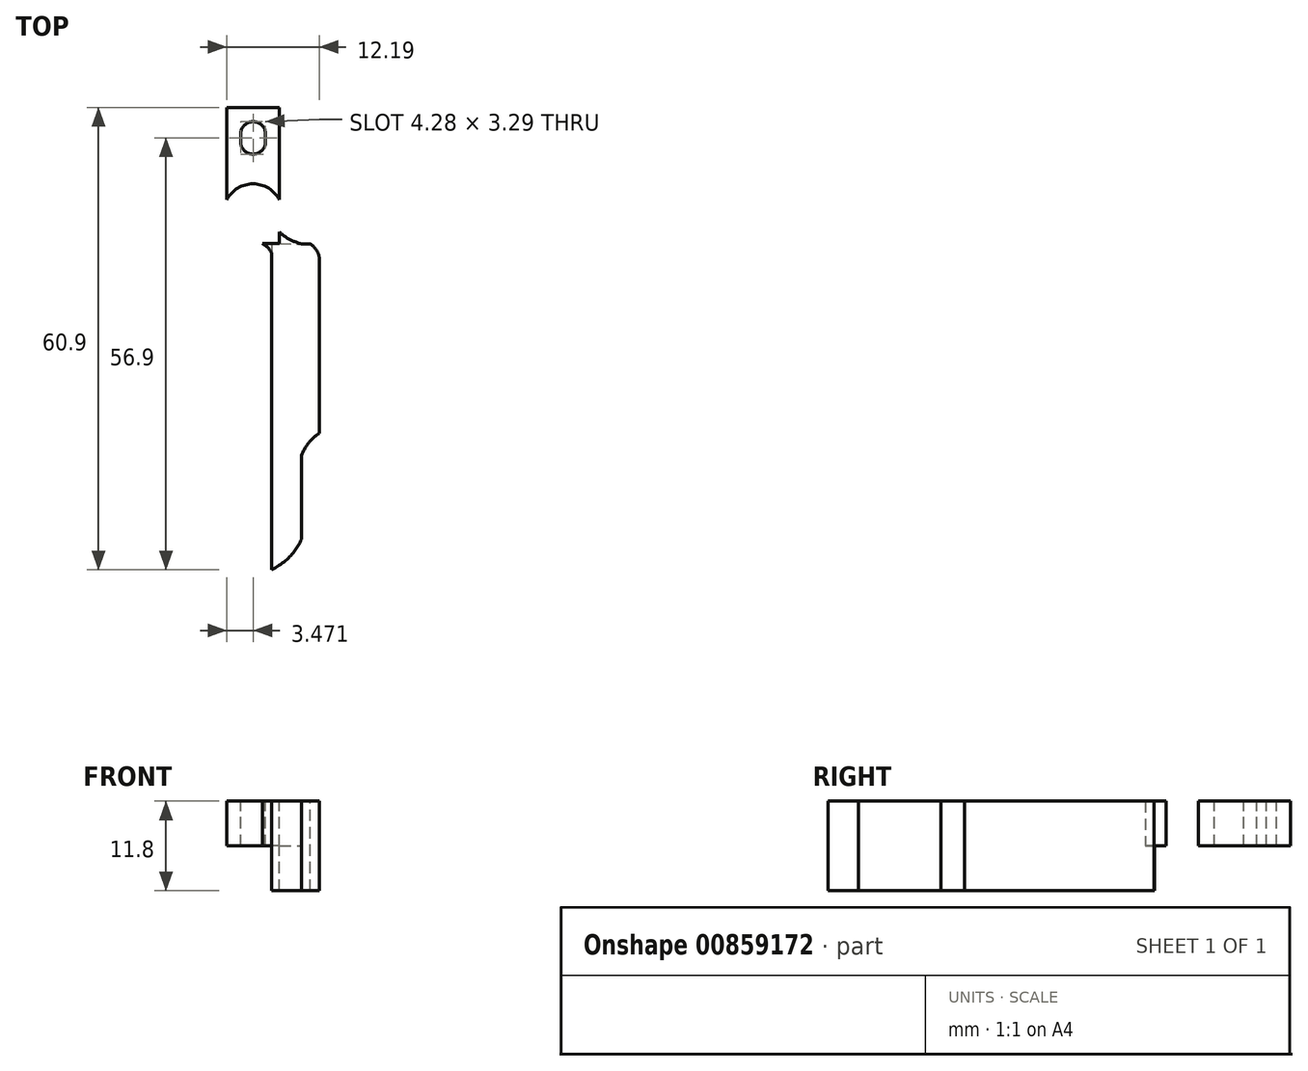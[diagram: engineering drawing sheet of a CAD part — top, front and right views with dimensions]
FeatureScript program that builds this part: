
annotation { "Feature Type Name" : "Feature", "Feature Type Description" : "" }
export const myFeature = defineFeature(function(context is Context, id is Id, definition is map)
    precondition{}
    {
        {
            var Q0;
            Q0=qCreatedBy(makeId("Top.planeOp"),FACE);
            var sketch = newSketch(context, id + "F0", { "sketchPlane" : qUnion([Q0])});
            skLineSegment(sketch, "E0.bottom", {"start": v(0, 0) * mm, "end": v(6.95, 0) * mm});
            skLineSegment(sketch, "E0.top", {"start": v(0, 17.9) * mm, "end": v(6.95, 17.9) * mm});
            skLineSegment(sketch, "E0.left", {"start": v(0, 0) * mm, "end": v(0, 17.9) * mm});
            skLineSegment(sketch, "E0.right", {"start": v(6.95, 0) * mm, "end": v(6.95, 17.9) * mm});
            skLineSegment(sketch, "E1", {"start": v(0, 0) * mm, "end": v(0, 7.85) * mm});
            skLineSegment(sketch, "E2", {"start": v(3.48, 0) * mm, "end": v(3.48, 7.85) * mm});
            skLineSegment(sketch, "E3", {"start": v(3.48, 7.85) * mm, "end": v(3.48, 6.9) * mm});
            skCircle(sketch, "E4", {"center": v(3.48, 3.92) * mm, "radius": 3.92 * mm});
            skLineSegment(sketch, "E5", {"start": v(3.47, 17.9) * mm, "end": v(3.47, 16.05) * mm});
            skLineSegment(sketch, "E6", {"start": v(3.47, 16.05) * mm, "end": v(3.48, 11.75) * mm});
            skLineSegment(sketch, "E7", {"start": v(3.47, 13.9) * mm, "end": v(3.47, 16.05) * mm});
            skLineSegment(sketch, "E8", {"start": v(3.48, 11.75) * mm, "end": v(3.47, 13.9) * mm});
            skLineSegment(sketch, "E9", {"start": v(4.55, 12.83) * mm, "end": v(4.55, 14.98) * mm});
            skLineSegment(sketch, "E10.bottom", {"start": v(3.48, 0) * mm, "end": v(1.03, 0) * mm});
            skLineSegment(sketch, "E10.top", {"start": v(3.48, -100) * mm, "end": v(1.03, -100) * mm});
            skLineSegment(sketch, "E10.left", {"start": v(3.48, 0) * mm, "end": v(3.48, -100) * mm});
            skLineSegment(sketch, "E10.right", {"start": v(1.03, 0) * mm, "end": v(1.03, -100) * mm});
            skLineSegment(sketch, "E11.bottom", {"start": v(3.48, 0) * mm, "end": v(5.93, 0) * mm});
            skLineSegment(sketch, "E11.top", {"start": v(3.48, -100) * mm, "end": v(5.93, -100) * mm});
            skLineSegment(sketch, "E11.right", {"start": v(5.93, 0) * mm, "end": v(5.93, -100) * mm});
            skLineSegment(sketch, "E12", {"start": v(5.93, 0) * mm, "end": v(5.93, 1.16) * mm});
            skLineSegment(sketch, "E13", {"start": v(1.03, 0) * mm, "end": v(1.02, 1.22) * mm});
            skLineSegment(sketch, "E14.bottom", {"start": v(6.95, 0) * mm, "end": v(9.83, -0.08) * mm});
            skLineSegment(sketch, "E14.left", {"start": v(6.95, 0) * mm, "end": v(6.95, 1.5) * mm});
            skLineSegment(sketch, "E15.right", {"start": v(5.93, -0.08) * mm, "end": v(5.93, -100) * mm});
            skLineSegment(sketch, "E16", {"start": v(3.48, 0) * mm, "end": v(3.48, -12.11) * mm});
            skLineSegment(sketch, "E17", {"start": v(3.48, 0) * mm, "end": v(3.48, -25) * mm});
            skLineSegment(sketch, "E18", {"start": v(3.48, -25) * mm, "end": v(1.03, -25) * mm});
            skLineSegment(sketch, "E19", {"start": v(1.03, -25) * mm, "end": v(1.03, -25.71) * mm});
            skLineSegment(sketch, "E20", {"start": v(1.03, -25) * mm, "end": v(1.03, -30) * mm});
            skLineSegment(sketch, "E21", {"start": v(5.93, -25) * mm, "end": v(5.93, -50) * mm});
            skPoint(sketch, "E21.startSnap0", {"position": v(2.25, -25) * mm});
            skLineSegment(sketch, "E22", {"start": v(5.93, -50) * mm, "end": v(9.83, -50.04) * mm});
            skLineSegment(sketch, "E23", {"start": v(3.48, -50) * mm, "end": v(1.03, -50) * mm});
            skLineSegment(sketch, "E24", {"start": v(5.93, -25) * mm, "end": v(9.83, -25) * mm});
            skLineSegment(sketch, "E25", {"start": v(5.93, -25) * mm, "end": v(5.93, -21.38) * mm});
            skLineSegment(sketch, "E26", {"start": v(5.93, -25) * mm, "end": v(5.93, -22.99) * mm});
            skLineSegment(sketch, "E27", {"start": v(3.48, -25) * mm, "end": v(3.48, -26.23) * mm});
            skLineSegment(sketch, "E28", {"start": v(5.93, -50) * mm, "end": v(5.93, -52.01) * mm});
            skLineSegment(sketch, "E29", {"start": v(3.48, -50) * mm, "end": v(3.48, -48.78) * mm});
            skLineSegment(sketch, "E30", {"start": v(5.93, -25) * mm, "end": v(5.93, -26.95) * mm});
            skLineSegment(sketch, "E31", {"start": v(3.48, -50) * mm, "end": v(5.93, -50) * mm});
            skLineSegment(sketch, "E32", {"start": v(3.48, 0) * mm, "end": v(3.48, -1.23) * mm});
            skLineSegment(sketch, "E33", {"start": v(6.95, 0) * mm, "end": v(6.95, 1.44) * mm});
            skFitSpline(sketch, "E34", {"points": [v(6.95, 1.5) * mm, v(9.83, -0.08) * mm], "startDerivative": vector(2.42, -2.4) * mm, "endDerivative": vector(3.34, -1.08) * mm});
            skLineSegment(sketch, "E35", {"start": v(1.03, 0) * mm, "end": v(1.03, -0.69) * mm});
            skLineSegment(sketch, "E36", {"start": v(1.03, 0) * mm, "end": v(1.03, -1) * mm});
            skLineSegment(sketch, "E37", {"start": v(5.92, 0) * mm, "end": v(5.93, -1.23) * mm});
            skFitSpline(sketch, "E38", {"points": [v(4.7, 0) * mm, v(5.93, -1.23) * mm], "startDerivative": vector(1.66, -0.95) * mm, "endDerivative": vector(0.86, -1.52) * mm});
            skLineSegment(sketch, "E39", {"start": v(5.93, -25) * mm, "end": v(5.93, -28.9) * mm});
            skLineSegment(sketch, "E40", {"start": v(3.48, -25) * mm, "end": v(5.93, -25) * mm});
            skLineSegment(sketch, "E41", {"start": v(5.93, -25) * mm, "end": v(5.93, -22.55) * mm});
            skLineSegment(sketch, "E42", {"start": v(5.93, -50) * mm, "end": v(5.93, -47.55) * mm});
            skFitSpline(sketch, "E43", {"points": [v(5.93, -47.55) * mm, v(3.48, -50) * mm], "startDerivative": vector(-2.07, -3.53) * mm, "endDerivative": vector(-2.94, -2.05) * mm});
            skLineSegment(sketch, "E44.left", {"start": v(5.93, -50) * mm, "end": v(5.93, -100) * mm});
            skLineSegment(sketch, "E45", {"start": v(9.83, -0.08) * mm, "end": v(9.83, -50.04) * mm});
            skLineSegment(sketch, "E46.bottom", {"start": v(9.83, -0.08) * mm, "end": v(12.2, -0.08) * mm});
            skLineSegment(sketch, "E46.top", {"start": v(9.83, -50.08) * mm, "end": v(12.2, -50.08) * mm});
            skLineSegment(sketch, "E46.left", {"start": v(9.83, -0.08) * mm, "end": v(9.83, -50.08) * mm});
            skLineSegment(sketch, "E46.right", {"start": v(12.2, -0.08) * mm, "end": v(12.2, -50.08) * mm});
            skLineSegment(sketch, "E47.bottom", {"start": v(5.93, -50) * mm, "end": v(8.3, -50) * mm});
            skLineSegment(sketch, "E47.top", {"start": v(5.93, -100) * mm, "end": v(8.3, -100) * mm});
            skLineSegment(sketch, "E47.right", {"start": v(8.3, -50) * mm, "end": v(8.3, -100) * mm});
            skLineSegment(sketch, "E48", {"start": v(8.3, -50) * mm, "end": v(12.2, -50.08) * mm});
            skLineSegment(sketch, "E49", {"start": v(8.3, -50) * mm, "end": v(8.3, -53.9) * mm});
            skFitSpline(sketch, "E50", {"points": [v(8.3, -53.9) * mm, v(10.24, -50.04) * mm], "startDerivative": vector(0.85, 4.55) * mm, "endDerivative": vector(3.1, 3.55) * mm});
            skCircle(sketch, "E51", {"center": v(3.48, 3.92) * mm, "radius": 3.28 * mm});
            skLineSegment(sketch, "E52", {"start": v(3.47, 13.9) * mm, "end": v(3.47, 12.9) * mm});
            skLineSegment(sketch, "E53", {"start": v(3.47, 13.9) * mm, "end": v(3.47, 14.9) * mm});
            skCircle(sketch, "E54", {"center": v(3.47, 13.4) * mm, "radius": 1.64 * mm});
            skArc(sketch, "E55", {"start": v(5.1, 14.7) * mm, "mid": v(1.83, 14.37) * mm, "end": v(5.1, 14.14) * mm});
            skLineSegment(sketch, "E56", {"start": v(3.48, 11.75) * mm, "end": v(1.27, 11.75) * mm});
            skLineSegment(sketch, "E57", {"start": v(3.48, 11.75) * mm, "end": v(5.93, 11.75) * mm});
            skLineSegment(sketch, "E58", {"start": v(3.47, 16.05) * mm, "end": v(1.21, 16.05) * mm});
            skLineSegment(sketch, "E59", {"start": v(3.47, 16.05) * mm, "end": v(5.69, 16.05) * mm});
            skLineSegment(sketch, "E60", {"start": v(5.11, 13.43) * mm, "end": v(5.1, 14.7) * mm});
            skLineSegment(sketch, "E61", {"start": v(1.84, 13.46) * mm, "end": v(1.83, 14.38) * mm});
            skLineSegment(sketch, "E62", {"start": v(9.83, -25) * mm, "end": v(12.2, -25) * mm});
            skFitSpline(sketch, "E63", {"points": [v(11.01, -0.08) * mm, v(12.2, -1.97) * mm], "startDerivative": vector(2.1, -1.32) * mm, "endDerivative": vector(0, -2.03) * mm});
            skLineSegment(sketch, "E64", {"start": v(5.93, -25) * mm, "end": v(5.93, -43) * mm});
            skLineSegment(sketch, "E65", {"start": v(5.93, -43) * mm, "end": v(9.83, -43) * mm});
            skFitSpline(sketch, "E66", {"points": [v(12.2, -25) * mm, v(9.83, -28.1) * mm], "startDerivative": vector(-3.43, -2.3) * mm, "endDerivative": vector(-1.13, -3.74) * mm});
            skFitSpline(sketch, "E67", {"points": [v(5.93, -43) * mm, v(9.83, -39) * mm], "startDerivative": vector(6.01, 3.16) * mm, "endDerivative": vector(2.1, 4.88) * mm});
            skSolve(sketch);
        }
        {
            var Q0;
            {var subQ0=sQuery(id+"F0.wireOp",EDGE,"E4");var subQ3=sQuery(id+"F0.wireOp",EDGE,"E0.right");var subQ10=makeQuery(id+"F0.imprint","INTERSECT",VERTEX,{"disambiguationData":[OD(0.0)],"derivedFrom":[subQ3,subQ0]});Q0=makeQuery(id+"F0.imprint","IMPRINT",FACE,{"disambiguationData":[TD([[makeQuery(id+"F0.imprint","IMPRINT",EDGE,{"disambiguationData":[TD([[subQ10,-1.0]])],"derivedFrom":subQ3}),1.0]])]});}
            var Q1;
            {var subQ0=sQuery(id+"F0.wireOp",EDGE,"E4");var subQ7=sQuery(id+"F0.wireOp",EDGE,"E1");var subQ10=makeQuery(id+"F0.imprint","INTERSECT",VERTEX,{"disambiguationData":[OD(0.0)],"derivedFrom":[subQ7,subQ0]});Q1=makeQuery(id+"F0.imprint","IMPRINT",FACE,{"disambiguationData":[TD([[makeQuery(id+"F0.imprint","IMPRINT",EDGE,{"disambiguationData":[TD([[subQ10,-1.0]])],"derivedFrom":subQ7}),-1.0]])]});}
            var Q2;
            {var subQ0=sQuery(id+"F0.wireOp",EDGE,"E1");var subQ1=sQuery(id+"F0.wireOp",EDGE,"E0.bottom");var subQ2=makeQuery(id+"F0.imprint","INTERSECT",VERTEX,{"derivedFrom":[subQ1,subQ0]});Q2=makeQuery(id+"F0.imprint","IMPRINT",FACE,{"disambiguationData":[TD([[makeQuery(id+"F0.imprint","IMPRINT",EDGE,{"disambiguationData":[TD([[subQ2,-1.0]])],"derivedFrom":subQ0}),-1.0]])]});}
            var Q3;
            {var subQ0=sQuery(id+"F0.wireOp",EDGE,"E10.bottom");Q3=makeQuery(id+"F0.imprint","IMPRINT",FACE,{"disambiguationData":[TD([[makeQuery(id+"F0.imprint","IMPRINT",EDGE,{"derivedFrom":subQ0}),-1.0]])]});}
            var Q4;
            {var subQ0=sQuery(id+"F0.wireOp",EDGE,"E4");var subQ1=sQuery(id+"F0.wireOp",EDGE,"E1");var subQ2=makeQuery(id+"F0.imprint","INTERSECT",VERTEX,{"disambiguationData":[OD(0.0)],"derivedFrom":[subQ1,subQ0]});Q4=makeQuery(id+"F0.imprint","IMPRINT",FACE,{"disambiguationData":[TD([[makeQuery(id+"F0.imprint","IMPRINT",EDGE,{"disambiguationData":[TD([[subQ2,-1.0]])],"derivedFrom":subQ1}),1.0]])]});}
            var Q5;
            {var subQ0=sQuery(id+"F0.wireOp",EDGE,"E4");var subQ1=sQuery(id+"F0.wireOp",EDGE,"E0.right");var subQ2=makeQuery(id+"F0.imprint","INTERSECT",VERTEX,{"disambiguationData":[OD(0.0)],"derivedFrom":[subQ1,subQ0]});Q5=makeQuery(id+"F0.imprint","IMPRINT",FACE,{"disambiguationData":[TD([[makeQuery(id+"F0.imprint","IMPRINT",EDGE,{"disambiguationData":[TD([[subQ2,-1.0]])],"derivedFrom":subQ1}),-1.0]])]});}
            var Q6;
            {var subQ5=sQuery(id+"F0.wireOp",EDGE,"E14.left");Q6=makeQuery(id+"F0.imprint","IMPRINT",FACE,{"disambiguationData":[TD([[makeQuery(id+"F0.imprint","IMPRINT",EDGE,{"derivedFrom":subQ5}),1.0]])]});}
            var Q7;
            {var subQ0=sQuery(id+"F0.wireOp",EDGE,"E11.bottom");var subQ5=makeQuery(id+"F0.imprint","INTERSECT",VERTEX,{"derivedFrom":[subQ0,sQuery(id+"F0.wireOp",EDGE,"E38")]});Q7=makeQuery(id+"F0.imprint","IMPRINT",FACE,{"disambiguationData":[TD([[makeQuery(id+"F0.imprint","IMPRINT",EDGE,{"disambiguationData":[TD([[subQ5,-1.0]])],"derivedFrom":subQ0}),1.0]])]});}
            var Q8;
            {var subQ3=sQuery(id+"F0.wireOp",EDGE,"E38");Q8=makeQuery(id+"F0.imprint","IMPRINT",FACE,{"disambiguationData":[TD([[makeQuery(id+"F0.imprint","IMPRINT",EDGE,{"derivedFrom":subQ3}),1.0]])]});}
            var Q9;
            Q9=makeQuery(id+"F0.imprint","IMPRINT",FACE,{"disambiguationData":[TD([[makeQuery(id+"F0.imprint","IMPRINT",EDGE,{"derivedFrom":sQuery(id+"F0.wireOp",EDGE,"E14.bottom")}),1.0]])]});
            extrude(context, id + "F1", {"entities" : qUnion([Q0, Q1, Q2, Q3, Q4, Q5, Q6, Q7, Q8, Q9]), "depth" : -5.9 * mm, "offsetDistance" : 25 * mm});
        }
        {
            var Q0;
            {var subQ15=sQuery(id+"F0.wireOp",EDGE,"E0.left");Q0=makeQuery(id+"F0.imprint","IMPRINT",FACE,{"disambiguationData":[TD([[makeQuery(id+"F0.imprint","IMPRINT",EDGE,{"derivedFrom":subQ15}),-1.0]])]});}
            extrude(context, id + "F2", {"entities" : qUnion([Q0]), "operationType" : NewBodyOperationType.ADD, "depth" : -2.5 * mm, "offsetDistance" : 25 * mm});
        }
        {
            var Q0;
            {var subQ1=sQuery(id+"F0.wireOp",EDGE,"E24");Q0=makeQuery(id+"F0.imprint","IMPRINT",FACE,{"disambiguationData":[TD([[makeQuery(id+"F0.imprint","IMPRINT",EDGE,{"derivedFrom":subQ1}),-1.0]])]});}
            var Q1;
            {var subQ0=sQuery(id+"F0.wireOp",EDGE,"E62");Q1=makeQuery(id+"F0.imprint","IMPRINT",FACE,{"disambiguationData":[TD([[makeQuery(id+"F0.imprint","IMPRINT",EDGE,{"derivedFrom":subQ0}),-1.0]])]});}
            var Q2;
            {var subQ2=sQuery(id+"F0.wireOp",EDGE,"E14.bottom");Q2=makeQuery(id+"F0.imprint","IMPRINT",FACE,{"disambiguationData":[TD([[makeQuery(id+"F0.imprint","IMPRINT",EDGE,{"derivedFrom":subQ2}),-1.0]])]});}
            var Q3;
            {var subQ0=sQuery(id+"F0.wireOp",EDGE,"E62");Q3=makeQuery(id+"F0.imprint","IMPRINT",FACE,{"disambiguationData":[TD([[makeQuery(id+"F0.imprint","IMPRINT",EDGE,{"derivedFrom":subQ0}),1.0]])]});}
            extrude(context, id + "F3", {"entities" : qUnion([Q0, Q1, Q2, Q3]), "operationType" : NewBodyOperationType.ADD, "depth" : -11.8 * mm, "offsetDistance" : 25 * mm});
        }
    });
